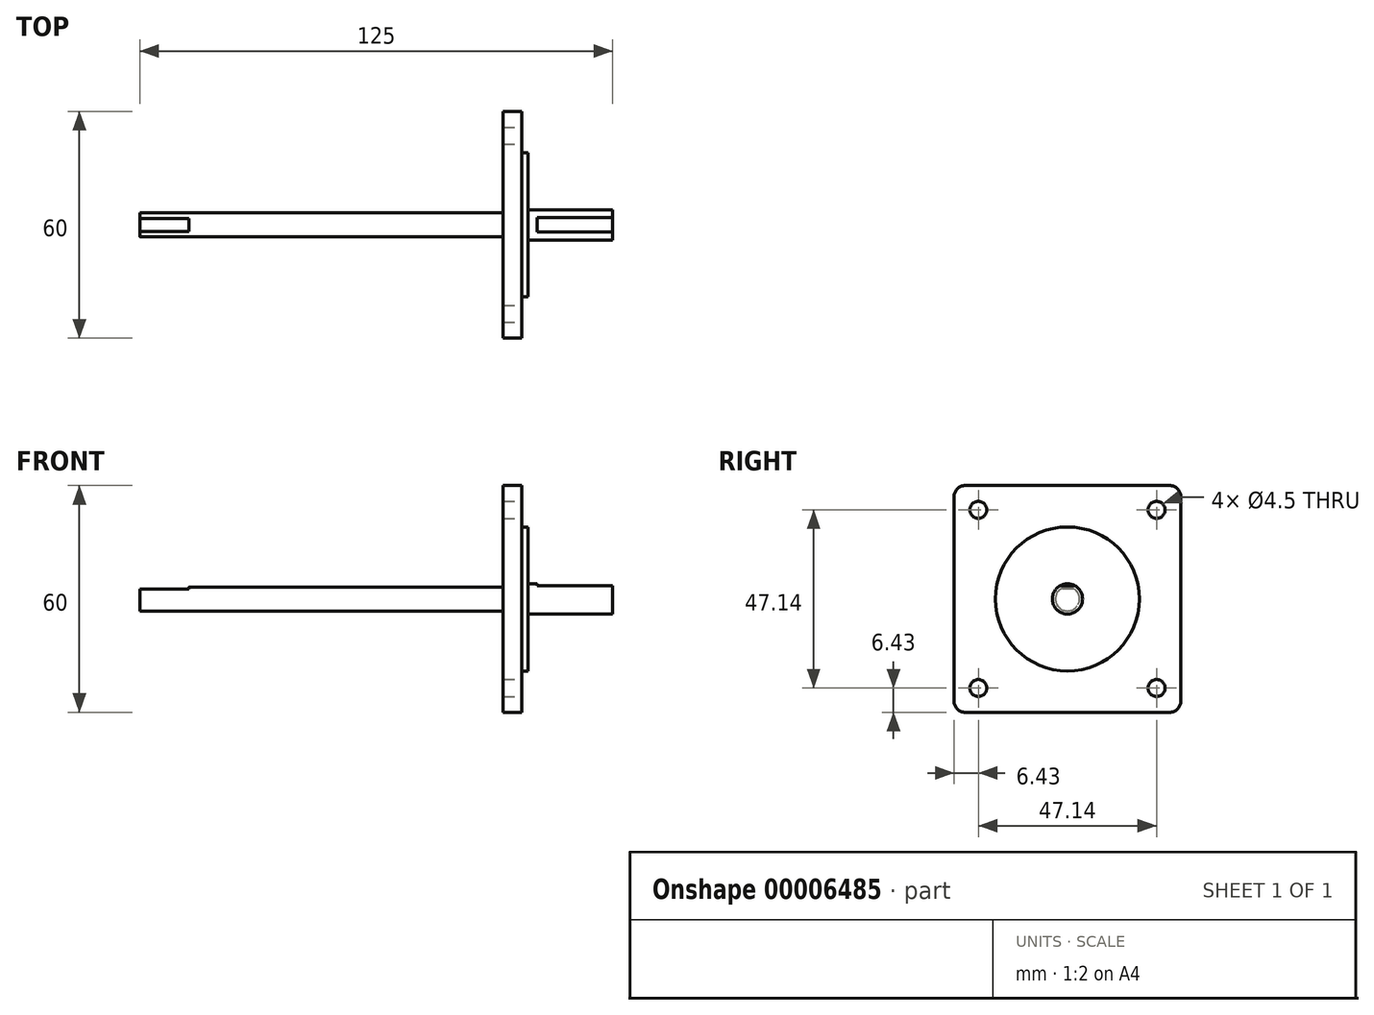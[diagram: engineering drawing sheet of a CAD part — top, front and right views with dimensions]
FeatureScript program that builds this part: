
annotation { "Feature Type Name" : "Feature", "Feature Type Description" : "" }
export const myFeature = defineFeature(function(context is Context, id is Id, definition is map)
    precondition{}
    {
        {
            var Q0;
            Q0=qCreatedBy(makeId("Right.planeOp"),FACE);
            var sketch = newSketch(context, id + "F0", { "sketchPlane" : qUnion([Q0])});
            skLineSegment(sketch, "E0.rect.bottom", {"start": v(27, 30) * mm, "end": v(-27, 30) * mm});
            skLineSegment(sketch, "E0.rect.top", {"start": v(27, -30) * mm, "end": v(-27, -30) * mm});
            skLineSegment(sketch, "E0.rect.left", {"start": v(30, 27) * mm, "end": v(30, -27) * mm});
            skLineSegment(sketch, "E0.rect.right", {"start": v(-30, 27) * mm, "end": v(-30, -27) * mm});
            skPoint(sketch, "E0.rect.middle", {"position": v(0, 0) * mm});
            skCircle(sketch, "E1", {"center": v(0, 0) * mm, "radius": 4 * mm});
            skCircle(sketch, "E2", {"center": v(0, 0) * mm, "radius": 19.05 * mm});
            skCircle(sketch, "E3", {"center": v(-23.57, 23.57) * mm, "radius": 2.25 * mm});
            skCircle(sketch, "E4.0.1.0", {"center": v(-23.57, -23.57) * mm, "radius": 2.25 * mm});
            skCircle(sketch, "E4.1.0.0", {"center": v(23.57, 23.57) * mm, "radius": 2.25 * mm});
            skCircle(sketch, "E4.1.1.0", {"center": v(23.57, -23.57) * mm, "radius": 2.25 * mm});
            skLineSegment(sketch, "E4.direction1", {"start": v(-23.57, 23.57) * mm, "end": v(23.57, 23.57) * mm, "construction": true});
            skLineSegment(sketch, "E4.direction2", {"start": v(-23.57, 23.57) * mm, "end": v(-23.57, -23.57) * mm, "construction": true});
            skLineSegment(sketch, "E5", {"start": v(0, 0) * mm, "end": v(0, 23.57) * mm, "construction": true});
            skLineSegment(sketch, "E6", {"start": v(0, 0) * mm, "end": v(-23.57, 0) * mm, "construction": true});
            skPoint(sketch, "E7.visualSharp", {"position": v(-30, 30) * mm});
            skArc(sketch, "E7.filletArc", {"start": v(-27, 30) * mm, "mid": v(-29.12, 29.12) * mm, "end": v(-30, 27) * mm});
            skPoint(sketch, "E8.visualSharp", {"position": v(30, 30) * mm});
            skArc(sketch, "E8.filletArc", {"start": v(30, 27) * mm, "mid": v(29.12, 29.12) * mm, "end": v(27, 30) * mm});
            skPoint(sketch, "E9.visualSharp", {"position": v(30, -30) * mm});
            skArc(sketch, "E9.filletArc", {"start": v(27, -30) * mm, "mid": v(29.12, -29.12) * mm, "end": v(30, -27) * mm});
            skPoint(sketch, "E10.visualSharp", {"position": v(-30, -30) * mm});
            skArc(sketch, "E10.filletArc", {"start": v(-30, -27) * mm, "mid": v(-29.12, -29.12) * mm, "end": v(-27, -30) * mm});
            skCircle(sketch, "E11", {"center": v(0, 0) * mm, "radius": 3.17 * mm});
            skSolve(sketch);
        }
        {
            var Q0;
            Q0=makeQuery(id+"F0.imprint","IMPRINT",FACE,{"disambiguationData":[TD([[makeQuery(id+"F0.imprint","IMPRINT",EDGE,{"derivedFrom":sQuery(id+"F0.wireOp",EDGE,"E0.rect.bottom")}),1.0]])]});
            var Q1;
            Q1=makeQuery(id+"F0.imprint","IMPRINT",FACE,{"disambiguationData":[TD([[makeQuery(id+"F0.imprint","IMPRINT",EDGE,{"derivedFrom":sQuery(id+"F0.wireOp",EDGE,"E1")}),-1.0]])]});
            var Q2;
            Q2=makeQuery(id+"F0.imprint","IMPRINT",FACE,{"disambiguationData":[TD([[makeQuery(id+"F0.imprint","IMPRINT",EDGE,{"derivedFrom":sQuery(id+"F0.wireOp",EDGE,"E1")}),1.0]])]});
            extrude(context, id + "F1", {"entities" : qUnion([Q0, Q1, Q2]), "oppositeDirection" : true, "depth" : 5 * mm});
        }
        {
            var Q0;
            Q0=makeQuery(id+"F0.imprint","IMPRINT",FACE,{"disambiguationData":[TD([[makeQuery(id+"F0.imprint","IMPRINT",EDGE,{"derivedFrom":sQuery(id+"F0.wireOp",EDGE,"E1")}),-1.0]])]});
            extrude(context, id + "F2", {"entities" : qUnion([Q0]), "operationType" : NewBodyOperationType.ADD, "depth" : 1.6 * mm});
        }
        {
            var Q0;
            Q0=makeQuery(id+"F0.imprint","IMPRINT",FACE,{"disambiguationData":[TD([[makeQuery(id+"F0.imprint","IMPRINT",EDGE,{"derivedFrom":sQuery(id+"F0.wireOp",EDGE,"E1")}),1.0]])]});
            var Q1;
            Q1=makeQuery(id+"F0.imprint","IMPRINT",FACE,{"disambiguationData":[TD([[makeQuery(id+"F0.imprint","IMPRINT",EDGE,{"derivedFrom":sQuery(id+"F0.wireOp",EDGE,"E11")}),1.0]])]});
            extrude(context, id + "F3", {"entities" : qUnion([Q0, Q1]), "depth" : 24 * mm});
        }
        {
            var Q0;
            Q0=makeQuery(id+"F0.imprint","IMPRINT",FACE,{"disambiguationData":[TD([[makeQuery(id+"F0.imprint","IMPRINT",EDGE,{"derivedFrom":sQuery(id+"F0.wireOp",EDGE,"E11")}),1.0]])]});
            extrude(context, id + "F4", {"entities" : qUnion([Q0]), "operationType" : NewBodyOperationType.ADD, "oppositeDirection" : true, "depth" : (88 + 13) * mm});
        }
        {
            var Q0;
            Q0=makeQuery(id+"F1.opExtrude","CAP_FACE",FACE,{"disambiguationData":[OSD([sQuery(id+"F0.wireOp",EDGE,"E0.rect.bottom"),sQuery(id+"F0.wireOp",EDGE,"E0.rect.top"),sQuery(id+"F0.wireOp",EDGE,"E0.rect.left"),sQuery(id+"F0.wireOp",EDGE,"E0.rect.right"),sQuery(id+"F0.wireOp",EDGE,"E3"),sQuery(id+"F0.wireOp",EDGE,"E4.0.1.0"),sQuery(id+"F0.wireOp",EDGE,"E4.1.0.0"),sQuery(id+"F0.wireOp",EDGE,"E4.1.1.0"),sQuery(id+"F0.wireOp",EDGE,"E7.filletArc"),sQuery(id+"F0.wireOp",EDGE,"E8.filletArc"),sQuery(id+"F0.wireOp",EDGE,"E9.filletArc"),sQuery(id+"F0.wireOp",EDGE,"E10.filletArc"),sQuery(id+"F0.wireOp",EDGE,"E11")])],"isStart":false});
            cPlane(context, id + "F5", {"entities" : qUnion([Q0]), "cplaneType" : CPlaneType.OFFSET, "offset" : (88 - 5) * mm, "width" : 150 * mm, "height" : 150 * mm});
        }
        {
            var Q0;
            Q0=qCreatedBy(id+"F5.planeOp",FACE);
            var sketch = newSketch(context, id + "F6", { "sketchPlane" : qUnion([Q0])});
            skPoint(sketch, "E12.0", {"position": v(0, 0) * mm});
            skCircle(sketch, "E13.0", {"center": v(0, 0) * mm, "radius": 3.17 * mm});
            skPoint(sketch, "E14.0", {"position": v(-30, 30) * mm});
            skPoint(sketch, "E15.0", {"position": v(30, 30) * mm});
            skPoint(sketch, "E16.0", {"position": v(30, -30) * mm});
            skPoint(sketch, "E17.0", {"position": v(-30, -30) * mm});
            skLineSegment(sketch, "E18.rect.bottom", {"start": v(15.05, 30) * mm, "end": v(-15.05, 30) * mm});
            skLineSegment(sketch, "E18.rect.top", {"start": v(15.05, -30) * mm, "end": v(-15.05, -30) * mm});
            skLineSegment(sketch, "E18.rect.left", {"start": v(30, 15.05) * mm, "end": v(30, -15.05) * mm});
            skLineSegment(sketch, "E18.rect.right", {"start": v(-30, 15.05) * mm, "end": v(-30, -15.05) * mm});
            skLineSegment(sketch, "E19", {"start": v(-17.05, 28) * mm, "end": v(-17.05, 22.05) * mm});
            skLineSegment(sketch, "E20", {"start": v(-22.05, 17.05) * mm, "end": v(-28, 17.05) * mm});
            skLineSegment(sketch, "E21", {"start": v(30, 0) * mm, "end": v(-30, 0) * mm, "construction": true});
            skLineSegment(sketch, "E22", {"start": v(0, 30) * mm, "end": v(0, -30) * mm, "construction": true});
            skPoint(sketch, "E23.visualSharp", {"position": v(-17.05, 17.05) * mm});
            skArc(sketch, "E23.filletArc", {"start": v(-22.05, 17.05) * mm, "mid": v(-18.52, 18.52) * mm, "end": v(-17.05, 22.05) * mm});
            skPoint(sketch, "E24.visualSharp", {"position": v(-17.05, 30) * mm});
            skArc(sketch, "E24.filletArc", {"start": v(-15.05, 30) * mm, "mid": v(-16.47, 29.41) * mm, "end": v(-17.05, 28) * mm});
            skPoint(sketch, "E25.visualSharp", {"position": v(-30, 17.05) * mm});
            skArc(sketch, "E25.filletArc", {"start": v(-28, 17.05) * mm, "mid": v(-29.41, 16.47) * mm, "end": v(-30, 15.05) * mm});
            skPoint(sketch, "E26.1.MirrorP", {"position": v(30, 17.05) * mm});
            skPoint(sketch, "E26.2.MirrorP", {"position": v(17.05, 30) * mm});
            skArc(sketch, "E26.3.MirrorCS", {"start": v(15.05, 30) * mm, "mid": v(16.47, 29.41) * mm, "end": v(17.05, 28) * mm});
            skArc(sketch, "E26.4.MirrorCS", {"start": v(22.05, 17.05) * mm, "mid": v(18.52, 18.52) * mm, "end": v(17.05, 22.05) * mm});
            skPoint(sketch, "E26.5.MirrorP", {"position": v(17.05, 17.05) * mm});
            skLineSegment(sketch, "E26.6.MirrorCS", {"start": v(17.05, 28) * mm, "end": v(17.05, 22.05) * mm});
            skArc(sketch, "E26.8.MirrorCS", {"start": v(28, 17.05) * mm, "mid": v(29.41, 16.47) * mm, "end": v(30, 15.05) * mm});
            skLineSegment(sketch, "E26.9.MirrorCS", {"start": v(22.05, 17.05) * mm, "end": v(28, 17.05) * mm});
            skArc(sketch, "E27.1.MirrorCS", {"start": v(-22.05, -17.05) * mm, "mid": v(-18.52, -18.52) * mm, "end": v(-17.05, -22.05) * mm});
            skPoint(sketch, "E27.2.MirrorP", {"position": v(-30, -17.05) * mm});
            skPoint(sketch, "E27.3.MirrorP", {"position": v(-17.05, -17.05) * mm});
            skArc(sketch, "E27.4.MirrorCS", {"start": v(-28, -17.05) * mm, "mid": v(-29.41, -16.47) * mm, "end": v(-30, -15.05) * mm});
            skLineSegment(sketch, "E27.5.MirrorCS", {"start": v(-22.05, -17.05) * mm, "end": v(-28, -17.05) * mm});
            skLineSegment(sketch, "E27.7.MirrorCS", {"start": v(-17.05, -28) * mm, "end": v(-17.05, -22.05) * mm});
            skPoint(sketch, "E27.8.MirrorP", {"position": v(-17.05, -30) * mm});
            skArc(sketch, "E27.9.MirrorCS", {"start": v(-15.05, -30) * mm, "mid": v(-16.47, -29.41) * mm, "end": v(-17.05, -28) * mm});
            skLineSegment(sketch, "E28.0.MirrorCS", {"start": v(22.05, -17.05) * mm, "end": v(28, -17.05) * mm});
            skLineSegment(sketch, "E28.2.MirrorCS", {"start": v(17.05, -28) * mm, "end": v(17.05, -22.05) * mm});
            skPoint(sketch, "E28.3.MirrorP", {"position": v(30, -17.05) * mm});
            skArc(sketch, "E28.5.MirrorCS", {"start": v(22.05, -17.05) * mm, "mid": v(18.52, -18.52) * mm, "end": v(17.05, -22.05) * mm});
            skArc(sketch, "E28.6.MirrorCS", {"start": v(15.05, -30) * mm, "mid": v(16.47, -29.41) * mm, "end": v(17.05, -28) * mm});
            skArc(sketch, "E28.8.MirrorCS", {"start": v(28, -17.05) * mm, "mid": v(29.41, -16.47) * mm, "end": v(30, -15.05) * mm});
            skPoint(sketch, "E28.9.MirrorP", {"position": v(17.05, -17.05) * mm});
            skPoint(sketch, "E28.10.MirrorP", {"position": v(17.05, -30) * mm});
            skSolve(sketch);
        }
        {
            var Q0;
            Q0=makeQuery(id+"F6.imprint","IMPRINT",FACE,{"disambiguationData":[TD([[makeQuery(id+"F6.imprint","IMPRINT",EDGE,{"derivedFrom":sQuery(id+"F6.wireOp",EDGE,"E13.0")}),1.0]])]});
            var Q1;
            Q1=makeQuery(id+"F1.opExtrude","CAP_FACE",FACE,{"disambiguationData":[OSD([sQuery(id+"F0.wireOp",EDGE,"E0.rect.bottom"),sQuery(id+"F0.wireOp",EDGE,"E0.rect.top"),sQuery(id+"F0.wireOp",EDGE,"E0.rect.left"),sQuery(id+"F0.wireOp",EDGE,"E0.rect.right"),sQuery(id+"F0.wireOp",EDGE,"E3"),sQuery(id+"F0.wireOp",EDGE,"E4.0.1.0"),sQuery(id+"F0.wireOp",EDGE,"E4.1.0.0"),sQuery(id+"F0.wireOp",EDGE,"E4.1.1.0"),sQuery(id+"F0.wireOp",EDGE,"E7.filletArc"),sQuery(id+"F0.wireOp",EDGE,"E8.filletArc"),sQuery(id+"F0.wireOp",EDGE,"E9.filletArc"),sQuery(id+"F0.wireOp",EDGE,"E10.filletArc"),sQuery(id+"F0.wireOp",EDGE,"E11")])],"isStart":false});
            extrude(context, id + "F7", {"entities" : qUnion([Q0]), "operationType" : NewBodyOperationType.ADD, "endBound" : BoundingType.UP_TO_SURFACE, "oppositeDirection" : true, "endBoundEntityFace" : qUnion([Q1]), "depth" : 131.37 * mm});
        }
        {
            var Q0;
            Q0=makeQuery(id+"F3.opExtrude","CAP_FACE",FACE,{"disambiguationData":[OSD([sQuery(id+"F0.wireOp",EDGE,"E1")])],"isStart":false});
            var sketch = newSketch(context, id + "F8", { "sketchPlane" : qUnion([Q0])});
            skLineSegment(sketch, "E29.rect.bottom", {"start": v(6.33, 8.2) * mm, "end": v(-6.33, 8.2) * mm});
            skLineSegment(sketch, "E29.rect.top", {"start": v(6.33, 3.5) * mm, "end": v(-6.33, 3.5) * mm});
            skLineSegment(sketch, "E29.rect.left", {"start": v(6.33, 8.2) * mm, "end": v(6.33, 3.5) * mm});
            skLineSegment(sketch, "E29.rect.right", {"start": v(-6.33, 8.2) * mm, "end": v(-6.33, 3.5) * mm});
            skPoint(sketch, "E29.rect.middle", {"position": v(0, 5.85) * mm});
            skLineSegment(sketch, "E30", {"start": v(0, -4) * mm, "end": v(0, 3.5) * mm, "construction": true});
            skSolve(sketch);
        }
        {
            var Q0;
            {var subQ0=makeQuery(id+"F3.opExtrude","CAP_EDGE",EDGE,{"disambiguationData":[OSD([sQuery(id+"F0.wireOp",EDGE,"E1")])],"isStart":false});var subQ1=sQuery(id+"F8.wireOp",EDGE,"E29.rect.top");var subQ3=makeQuery(id+"F8.imprint","INTERSECT",VERTEX,{"disambiguationData":[OD(0.0)],"derivedFrom":[subQ0,subQ1]});Q0=makeQuery(id+"F8.imprint","IMPRINT",FACE,{"disambiguationData":[TD([[makeQuery(id+"F8.imprint","IMPRINT",EDGE,{"disambiguationData":[TD([[subQ3,-1.0]])],"derivedFrom":subQ1}),-1.0]])]});}
            extrude(context, id + "F9", {"entities" : qUnion([Q0]), "operationType" : NewBodyOperationType.REMOVE, "oppositeDirection" : true, "depth" : 20 * mm});
        }
        {
            var Q0;
            Q0=makeQuery(id+"F4.opExtrude","CAP_FACE",FACE,{"disambiguationData":[OSD([sQuery(id+"F0.wireOp",EDGE,"E11")])],"isStart":false});
            var sketch = newSketch(context, id + "F10", { "sketchPlane" : qUnion([Q0])});
            skLineSegment(sketch, "E31", {"start": v(0, -3.17) * mm, "end": v(0, 2.68) * mm, "construction": true});
            skLineSegment(sketch, "E32", {"start": v(-1.71, 2.68) * mm, "end": v(1.71, 2.68) * mm});
            skSolve(sketch);
        }
        {
            var Q0;
            {var subQ1=sQuery(id+"F10.wireOp",EDGE,"E32");Q0=makeQuery(id+"F10.imprint","IMPRINT",FACE,{"disambiguationData":[TD([[makeQuery(id+"F10.imprint","IMPRINT",EDGE,{"derivedFrom":subQ1}),1.0]])]});}
            extrude(context, id + "F11", {"entities" : qUnion([Q0]), "operationType" : NewBodyOperationType.REMOVE, "oppositeDirection" : true, "depth" : 13 * mm});
        }
    });
